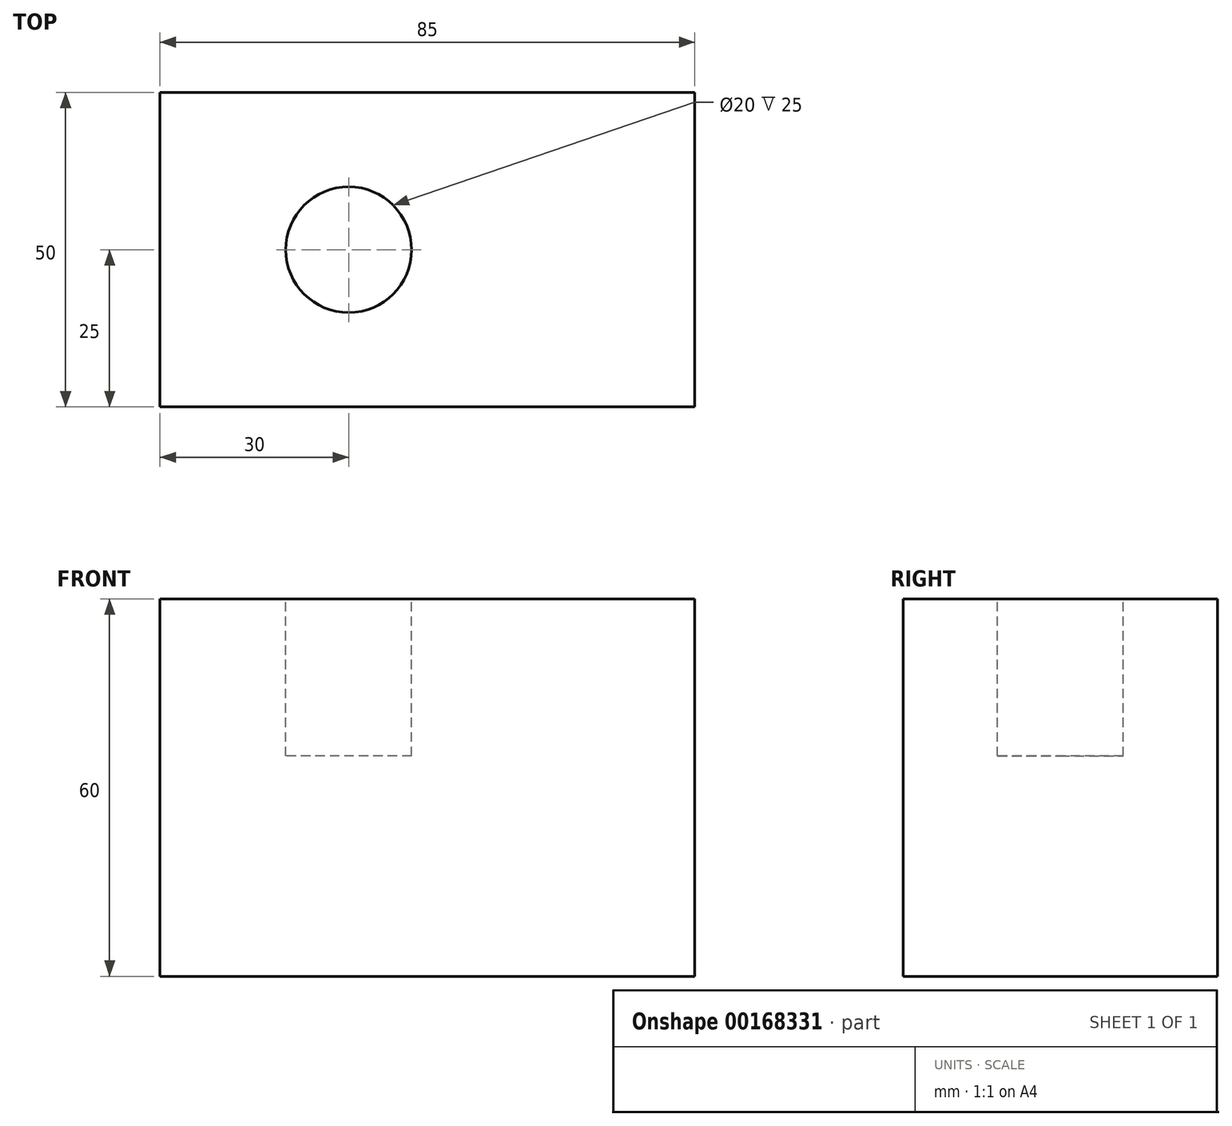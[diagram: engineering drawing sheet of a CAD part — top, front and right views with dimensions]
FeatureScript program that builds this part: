
annotation { "Feature Type Name" : "Feature", "Feature Type Description" : "" }
export const myFeature = defineFeature(function(context is Context, id is Id, definition is map)
    precondition{}
    {
        {
            var Q0;
            Q0=qCreatedBy(makeId("Top.planeOp"),FACE);
            var sketch = newSketch(context, id + "F0", { "sketchPlane" : qUnion([Q0])});
            skLineSegment(sketch, "E0.bottom", {"start": v(30, 25) * mm, "end": v(-30, 25) * mm});
            skLineSegment(sketch, "E0.top", {"start": v(30, -25) * mm, "end": v(-30, -25) * mm});
            skLineSegment(sketch, "E0.left", {"start": v(30, 25) * mm, "end": v(30, -25) * mm});
            skLineSegment(sketch, "E0.right", {"start": v(-30, 25) * mm, "end": v(-30, -25) * mm});
            skPoint(sketch, "E0.middle", {"position": v(0, 0) * mm});
            skSolve(sketch);
        }
        {
            var Q0;
            Q0 = qSketchRegion(id + "F0", true);
            extrude(context, id + "F1", {"entities" : qUnion([Q0]), "depth" : 60 * mm});
        }
        {
            var Q0;
            Q0=makeQuery(id+"F1.opExtrude","CAP_FACE",FACE,{"disambiguationData":[OSD([sQuery(id+"F0.wireOp",EDGE,"E0.bottom"),sQuery(id+"F0.wireOp",EDGE,"E0.top"),sQuery(id+"F0.wireOp",EDGE,"E0.left"),sQuery(id+"F0.wireOp",EDGE,"E0.right")])],"isStart":false});
            var sketch = newSketch(context, id + "F2", { "sketchPlane" : qUnion([Q0])});
            skCircle(sketch, "E1", {"center": v(0, 0) * mm, "radius": 10 * mm});
            skSolve(sketch);
        }
        {
            var Q0;
            Q0 = qSketchRegion(id + "F2", true);
            extrude(context, id + "F3", {"entities" : qUnion([Q0]), "operationType" : NewBodyOperationType.REMOVE, "oppositeDirection" : true, "depth" : 25 * mm});
        }
        {
            var Q0;
            Q0=makeQuery(id+"F1.opExtrude","SWEPT_FACE",FACE,{"disambiguationData":[OSD([sQuery(id+"F0.wireOp",EDGE,"E0.left")])]});
            extrude(context, id + "F4", {"entities" : qUnion([Q0]), "operationType" : NewBodyOperationType.ADD, "depth" : 25 * mm});
        }
    });
